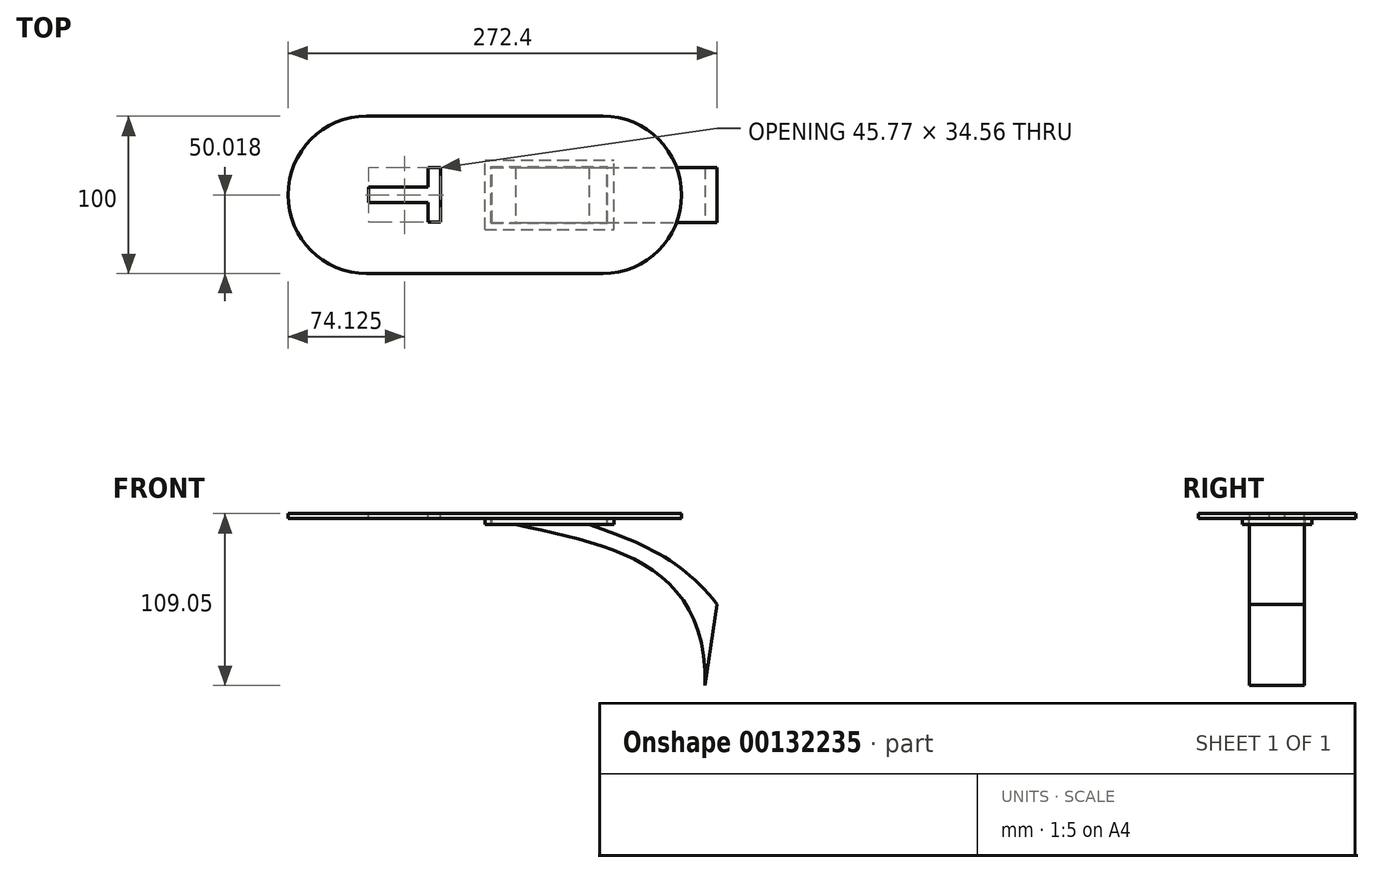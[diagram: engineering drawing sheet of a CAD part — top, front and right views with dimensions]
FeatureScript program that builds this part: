
annotation { "Feature Type Name" : "Feature", "Feature Type Description" : "" }
export const myFeature = defineFeature(function(context is Context, id is Id, definition is map)
    precondition{}
    {
        {
            var Q0;
            Q0=qCreatedBy(makeId("Top.planeOp"),FACE);
            var sketch = newSketch(context, id + "F0", { "sketchPlane" : qUnion([Q0])});
            skLineSegment(sketch, "E0.bottom", {"start": v(75, -50) * mm, "end": v(-75, -50) * mm});
            skLineSegment(sketch, "E0.top", {"start": v(75, 50) * mm, "end": v(-75, 50) * mm});
            skLineSegment(sketch, "E0.left", {"start": v(75, -50) * mm, "end": v(75, 50) * mm});
            skLineSegment(sketch, "E0.right", {"start": v(-75, -50) * mm, "end": v(-75, 50) * mm});
            skPoint(sketch, "E0.middle", {"position": v(0, 0) * mm});
            skPoint(sketch, "E1.middle", {"position": v(-75, 50) * mm});
            skArc(sketch, "E2", {"start": v(-75, 50) * mm, "mid": v(-125, 0) * mm, "end": v(-75, -50) * mm});
            skArc(sketch, "E3.MirrorCS", {"start": v(75, 50) * mm, "mid": v(125, 0) * mm, "end": v(75, -50) * mm});
            skPoint(sketch, "E4.MirrorP", {"position": v(75, 50) * mm});
            skSolve(sketch);
        }
        {
            var Q0;
            Q0 = qSketchRegion(id + "F0", true);
            extrude(context, id + "F1", {"entities" : qUnion([Q0]), "depth" : 3 * mm});
        }
        {
            var Q0;
            Q0=makeQuery(id+"F1.opExtrude","CAP_FACE",FACE,{"disambiguationData":[OSD([sQuery(id+"F0.wireOp",EDGE,"E0.bottom"),sQuery(id+"F0.wireOp",EDGE,"E0.top"),sQuery(id+"F0.wireOp",EDGE,"E2"),sQuery(id+"F0.wireOp",EDGE,"E3.MirrorCS")])],"isStart":true});
            var sketch = newSketch(context, id + "F2", { "sketchPlane" : qUnion([Q0])});
            skLineSegment(sketch, "E5.bottom", {"start": v(0, 22) * mm, "end": v(82, 22) * mm});
            skLineSegment(sketch, "E5.top", {"start": v(0, -22) * mm, "end": v(82, -22) * mm});
            skLineSegment(sketch, "E5.left", {"start": v(0, 22) * mm, "end": v(0, -22) * mm});
            skLineSegment(sketch, "E5.right", {"start": v(82, 22) * mm, "end": v(82, -22) * mm});
            skLineSegment(sketch, "E6.bottom", {"start": v(4, 18) * mm, "end": v(78, 18) * mm});
            skLineSegment(sketch, "E6.top", {"start": v(4, -18) * mm, "end": v(78, -18) * mm});
            skLineSegment(sketch, "E6.left", {"start": v(4, 18) * mm, "end": v(4, -18) * mm});
            skLineSegment(sketch, "E6.right", {"start": v(78, 18) * mm, "end": v(78, -18) * mm});
            skSolve(sketch);
        }
        {
            var Q0;
            Q0 = qSketchRegion(id + "F2", true);
            extrude(context, id + "F3", {"entities" : qUnion([Q0]), "operationType" : NewBodyOperationType.ADD, "depth" : 4 * mm});
        }
        {
            var Q0;
            Q0=makeQuery(id+"F3.boolean.opBoolean","SPLIT",FACE,{"disambiguationData":[TD([makeQuery(id+"F3.opExtrude","SWEPT_FACE",FACE,{"disambiguationData":[OSD([sQuery(id+"F2.wireOp",EDGE,"E6.bottom")])]})])],"derivedFrom":makeQuery(id+"F1.opExtrude","CAP_FACE",FACE,{"disambiguationData":[OSD([sQuery(id+"F0.wireOp",EDGE,"E0.bottom"),sQuery(id+"F0.wireOp",EDGE,"E0.top"),sQuery(id+"F0.wireOp",EDGE,"E2"),sQuery(id+"F0.wireOp",EDGE,"E3.MirrorCS")])],"isStart":true})});
            var sketch = newSketch(context, id + "F4", { "sketchPlane" : qUnion([Q0])});
            skLineSegment(sketch, "E7.0", {"start": v(4.5, 17.5) * mm, "end": v(77.5, 17.5) * mm});
            skLineSegment(sketch, "E7.1", {"start": v(4.5, 17.5) * mm, "end": v(4.5, -17.5) * mm});
            skLineSegment(sketch, "E7.2", {"start": v(4.5, -17.5) * mm, "end": v(77.5, -17.5) * mm});
            skLineSegment(sketch, "E7.3", {"start": v(77.5, 17.5) * mm, "end": v(77.5, -17.5) * mm});
            skSolve(sketch);
        }
        {
            var Q0;
            Q0=makeQuery(id+"F4.imprint","IMPRINT",FACE,{"disambiguationData":[TD([[makeQuery(id+"F4.imprint","IMPRINT",EDGE,{"derivedFrom":sQuery(id+"F4.wireOp",EDGE,"E7.0")}),-1.0]])]});
            extrude(context, id + "F5", {"entities" : qUnion([Q0]), "depth" : 4 * mm});
        }
        {
            var Q0;
            Q0=makeQuery(id+"F5.opExtrude","SWEPT_FACE",FACE,{"disambiguationData":[OSD([sQuery(id+"F4.wireOp",EDGE,"E7.0")])]});
            var sketch = newSketch(context, id + "F6", { "sketchPlane" : qUnion([Q0])});
            skFitSpline(sketch, "E8", {"points": [v(19.5, -4) * mm, v(139.86, -106.05) * mm], "startDerivative": vector(188.67, -38.53) * mm, "endDerivative": vector(-4.84, -230) * mm});
            skFitSpline(sketch, "E9", {"points": [v(66.21, -4) * mm, v(147.4, -54.68) * mm], "startDerivative": vector(103.47, -33.48) * mm, "endDerivative": vector(59.28, -79.76) * mm});
            skLineSegment(sketch, "E10", {"start": v(147.4, -54.68) * mm, "end": v(139.86, -106.05) * mm});
            skSolve(sketch);
        }
        {
            var Q0;
            {var subQ0=sQuery(id+"F6.wireOp",EDGE,"E8");Q0=makeQuery(id+"F6.imprint","IMPRINT",FACE,{"disambiguationData":[TD([[makeQuery(id+"F6.imprint","IMPRINT",EDGE,{"derivedFrom":subQ0}),1.0]])]});}
            var Q1;
            Q1=makeQuery(id+"F5.opExtrude","SWEPT_FACE",FACE,{"disambiguationData":[OSD([sQuery(id+"F4.wireOp",EDGE,"E7.2")])]});
            extrude(context, id + "F7", {"entities" : qUnion([Q0]), "operationType" : NewBodyOperationType.ADD, "endBound" : BoundingType.UP_TO_SURFACE, "oppositeDirection" : true, "endBoundEntityFace" : qUnion([Q1]), "depth" : 25 * mm});
        }
        {
            var Q0;
            Q0=makeQuery(id+"F1.opExtrude","CAP_FACE",FACE,{"disambiguationData":[OSD([sQuery(id+"F0.wireOp",EDGE,"E0.bottom"),sQuery(id+"F0.wireOp",EDGE,"E0.top"),sQuery(id+"F0.wireOp",EDGE,"E2"),sQuery(id+"F0.wireOp",EDGE,"E3.MirrorCS")])],"isStart":false});
            var sketch = newSketch(context, id + "F8", { "sketchPlane" : qUnion([Q0])});
            skText(sketch, "E11", { "text": "T", "fontName": "OpenSans-Bold.ttf"});
            const initialGuessF8  = {"E11": [-0.07376, 0.01858, 0, -1, 0.04616]};
            skSetInitialGuess(sketch, initialGuessF8);
            skSolve(sketch);
        }
        {
            var Q0;
            Q0 = qSketchRegion(id + "F8", true);
            extrude(context, id + "F9", {"entities" : qUnion([Q0]), "operationType" : NewBodyOperationType.REMOVE, "endBound" : BoundingType.UP_TO_NEXT, "oppositeDirection" : true, "depth" : 25 * mm});
        }
    });
